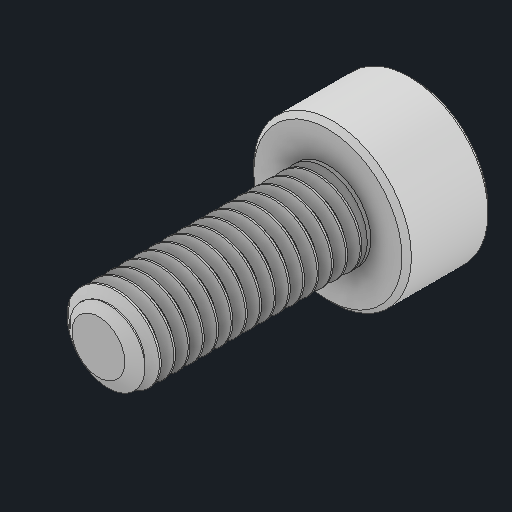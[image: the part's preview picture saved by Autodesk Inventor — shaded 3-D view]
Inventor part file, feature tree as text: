
AUTODESK INVENTOR PART (.ipt)
format: ipt  version: 2025 (Build 290162000, 162)  size: 636,416 bytes
history: native  units: mm
features: revolve x1
ambient origin geometry x8: Origin, YZ Plane, XZ Plane, XY Plane, X Axis, Y Axis, Z Axis, Center Point
bodies: Solid1 (feature_tree)
feature tree (1):
  revolve  "Revolve1"  [1 undecoded]
note: 1 required parameter value undecoded (feature->parameter linkage not recoverable at this tier; creation-order binding heuristic only, values carry confidence <= 0.55)
